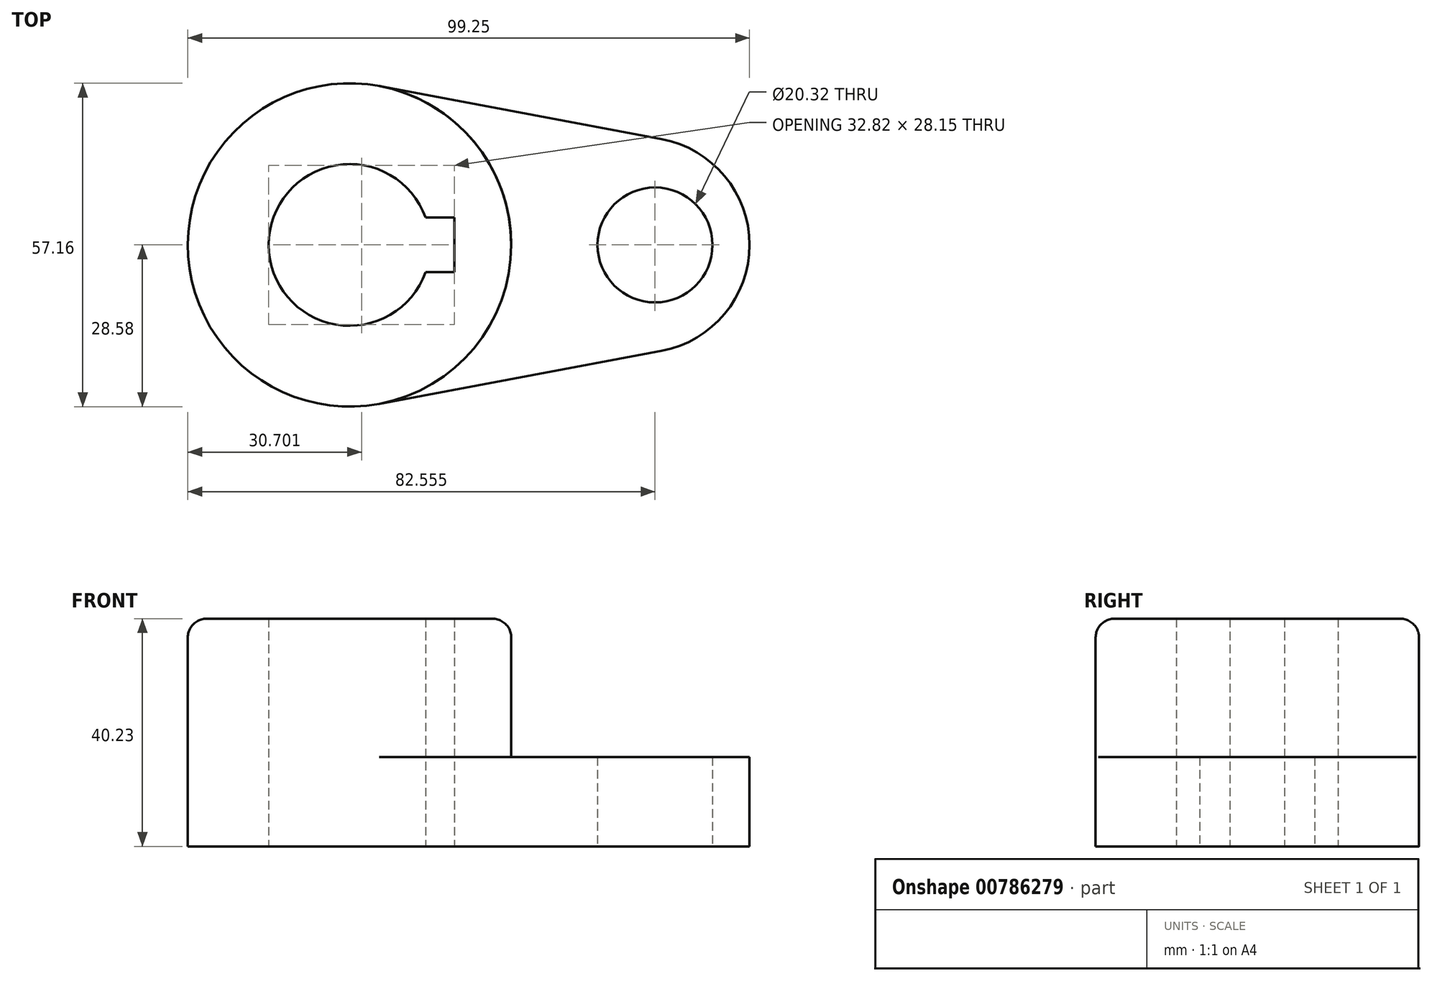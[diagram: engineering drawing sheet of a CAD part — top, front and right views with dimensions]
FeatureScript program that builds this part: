
annotation { "Feature Type Name" : "Feature", "Feature Type Description" : "" }
export const myFeature = defineFeature(function(context is Context, id is Id, definition is map)
    precondition{}
    {
        {
            var Q0;
            Q0=qCreatedBy(makeId("Top.planeOp"),FACE);
            var sketch = newSketch(context, id + "F0", { "sketchPlane" : qUnion([Q0])});
            skCircle(sketch, "E0", {"center": v(0, 0) * mm, "radius": 28.58 * mm});
            skCircle(sketch, "E1", {"center": v(0, 0) * mm, "radius": 14.29 * mm});
            skCircle(sketch, "E2", {"center": v(53.98, 0) * mm, "radius": 10.16 * mm});
            skLineSegment(sketch, "E3", {"start": v(5.27, 28.08) * mm, "end": v(55.14, 18.72) * mm});
            skLineSegment(sketch, "E4.MirrorCS", {"start": v(5.27, -28.08) * mm, "end": v(55.14, -18.72) * mm});
            skArc(sketch, "E5", {"start": v(55.14, -18.72) * mm, "mid": v(70.67, 0) * mm, "end": v(55.14, 18.72) * mm});
            skLineSegment(sketch, "E6.bottom", {"start": v(18.53, 4.83) * mm, "end": v(-18.53, 4.83) * mm});
            skLineSegment(sketch, "E6.top", {"start": v(18.53, -4.83) * mm, "end": v(-18.53, -4.83) * mm});
            skLineSegment(sketch, "E6.left", {"start": v(18.53, 4.83) * mm, "end": v(18.53, -4.83) * mm});
            skLineSegment(sketch, "E6.right", {"start": v(-18.53, 4.83) * mm, "end": v(-18.53, -4.83) * mm});
            skSolve(sketch);
        }
        {
            var Q0;
            Q0=makeQuery(id+"F0.imprint","IMPRINT",FACE,{"disambiguationData":[TD([[makeQuery(id+"F0.imprint","IMPRINT",EDGE,{"derivedFrom":sQuery(id+"F0.wireOp",EDGE,"E2")}),-1.0]])]});
            extrude(context, id + "F1", {"entities" : qUnion([Q0]), "depth" : 15.77 * mm, "offsetDistance" : 25.4 * mm});
        }
        {
            var Q0;
            {var subQ8=sQuery(id+"F0.wireOp",EDGE,"E6.left");Q0=makeQuery(id+"F0.imprint","IMPRINT",FACE,{"disambiguationData":[TD([[makeQuery(id+"F0.imprint","IMPRINT",EDGE,{"derivedFrom":subQ8}),1.0]])]});}
            var Q1;
            {var subQ5=sQuery(id+"F0.wireOp",EDGE,"E6.right");Q1=makeQuery(id+"F0.imprint","IMPRINT",FACE,{"disambiguationData":[TD([[makeQuery(id+"F0.imprint","IMPRINT",EDGE,{"derivedFrom":subQ5}),1.0]])]});}
            extrude(context, id + "F2", {"entities" : qUnion([Q0, Q1]), "operationType" : NewBodyOperationType.ADD, "depth" : 40.23 * mm, "offsetDistance" : 25.4 * mm});
        }
        {
            var Q0;
            Q0=makeQuery(id+"F2.opExtrude","CAP_EDGE",EDGE,{"disambiguationData":[OSD([sQuery(id+"F0.wireOp",EDGE,"E0")])],"isStart":false});
            fillet(context, id + "F3", {"entities" : qUnion([Q0]), "radius" : 3.3 * mm, "tangentPropagation" : true, "allowEdgeOverflow" : false});
        }
    });
